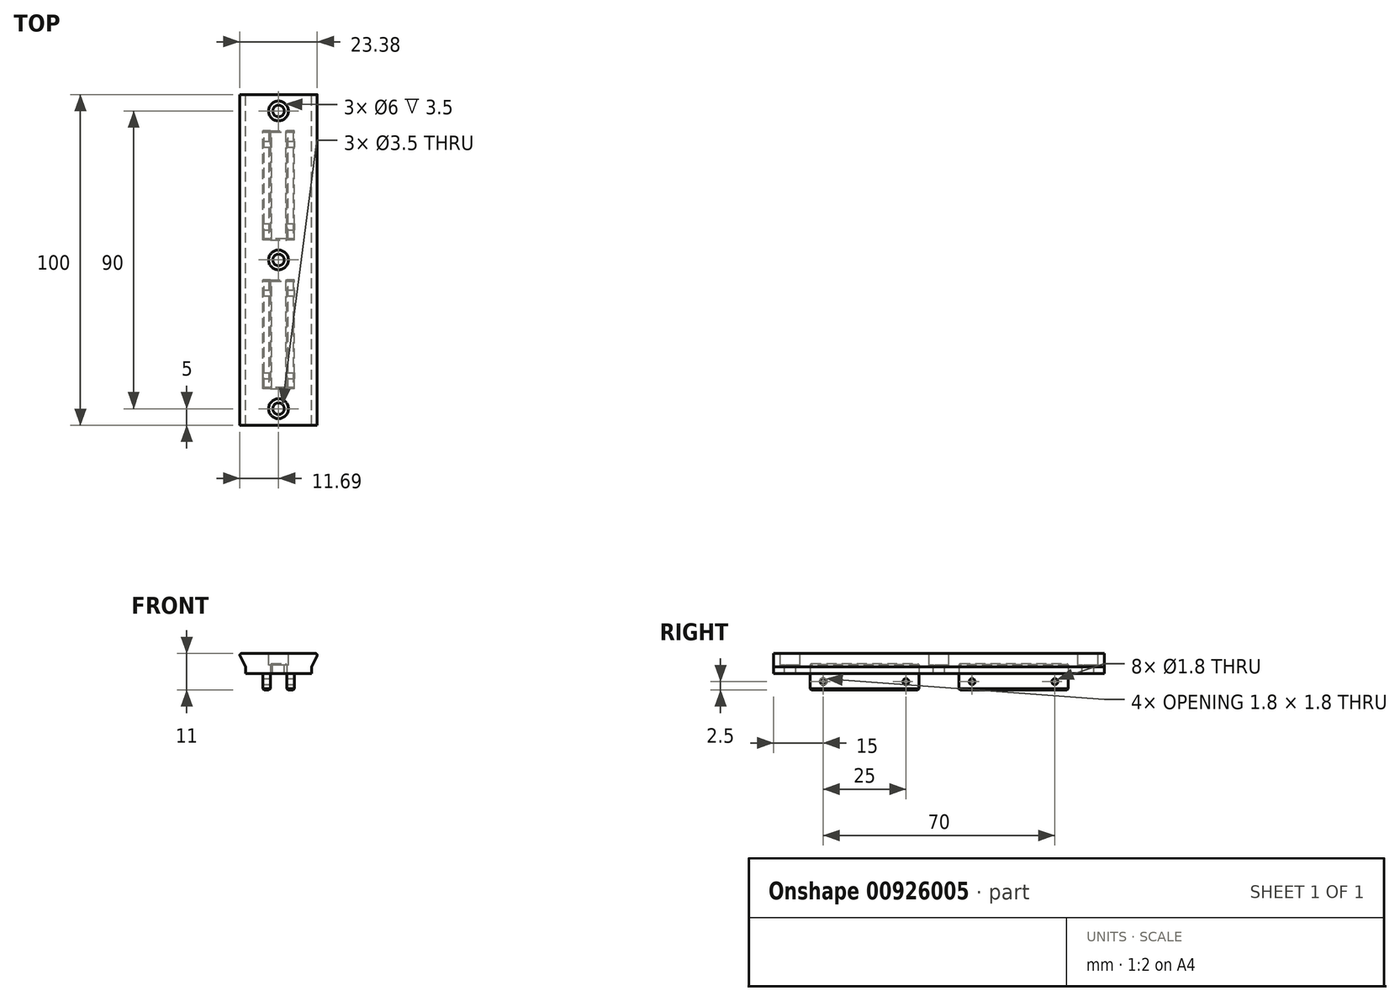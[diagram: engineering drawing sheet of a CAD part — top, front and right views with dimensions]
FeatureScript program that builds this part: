
annotation { "Feature Type Name" : "Feature", "Feature Type Description" : "" }
export const myFeature = defineFeature(function(context is Context, id is Id, definition is map)
    precondition{}
    {
        {
            var Q0;
            Q0=qCreatedBy(makeId("Front.planeOp"),FACE);
            var sketch = newSketch(context, id + "F0", { "sketchPlane" : qUnion([Q0])});
            skLineSegment(sketch, "E0.top", {"start": v(4.75, -2.5) * mm, "end": v(-4.75, -2.5) * mm});
            skLineSegment(sketch, "E0.left", {"start": v(4.75, 2.5) * mm, "end": v(4.75, -2.5) * mm});
            skLineSegment(sketch, "E0.right", {"start": v(-4.75, 2.5) * mm, "end": v(-4.75, -2.5) * mm});
            skPoint(sketch, "E0.middle", {"position": v(0, 0) * mm});
            skLineSegment(sketch, "E1.left", {"start": v(10, 4.5) * mm, "end": v(10, 2.5) * mm});
            skLineSegment(sketch, "E1.right", {"start": v(-10, 4.5) * mm, "end": v(-10, 2.5) * mm});
            skPoint(sketch, "E1.middle", {"position": v(0, 2.5) * mm});
            skLineSegment(sketch, "E2", {"start": v(-4.75, 2.5) * mm, "end": v(-10, 2.5) * mm});
            skLineSegment(sketch, "E3", {"start": v(4.75, 2.5) * mm, "end": v(10, 2.5) * mm});
            skPoint(sketch, "E4.orphan", {"position": v(-10, 0.5) * mm});
            skPoint(sketch, "E5.orphan", {"position": v(10, 0.5) * mm});
            skLineSegment(sketch, "E6.bottom", {"start": v(10, 8.5) * mm, "end": v(-10, 8.5) * mm});
            skPoint(sketch, "E6.middle", {"position": v(0, 4.5) * mm});
            skLineSegment(sketch, "E7.bottom", {"start": v(-10, 8.5) * mm, "end": v(-6, 8.5) * mm});
            skLineSegment(sketch, "E8.bottom", {"start": v(10, 8.5) * mm, "end": v(6, 8.5) * mm});
            skLineSegment(sketch, "E9.bottom", {"start": v(-2.5, -2.5) * mm, "end": v(2.5, -2.5) * mm});
            skLineSegment(sketch, "E9.top", {"start": v(-2.5, 2.5) * mm, "end": v(2.5, 2.5) * mm});
            skLineSegment(sketch, "E9.left", {"start": v(-2.5, -2.5) * mm, "end": v(-2.5, 2.5) * mm});
            skLineSegment(sketch, "E9.right", {"start": v(2.5, -2.5) * mm, "end": v(2.5, 2.5) * mm});
            skLineSegment(sketch, "E10", {"start": v(-10, 8.5) * mm, "end": v(-12, 8.5) * mm});
            skLineSegment(sketch, "E11", {"start": v(10, 8.5) * mm, "end": v(12, 8.5) * mm});
            skLineSegment(sketch, "E12", {"start": v(-12, 8.5) * mm, "end": v(-10, 4.5) * mm});
            skLineSegment(sketch, "E13", {"start": v(12, 8.5) * mm, "end": v(10, 4.5) * mm});
            skSolve(sketch);
        }
        {
            var Q0;
            {var subQ0=sQuery(id+"F0.wireOp",EDGE,"E0.left");Q0=makeQuery(id+"F0.imprint","IMPRINT",FACE,{"disambiguationData":[TD([[makeQuery(id+"F0.imprint","IMPRINT",EDGE,{"derivedFrom":subQ0}),-1.0]])]});}
            extrude(context, id + "F1", {"entities" : qUnion([Q0]), "depth" : 100 * mm, "offsetDistance" : 25 * mm});
        }
        {
            var Q0;
            Q0=makeQuery(id+"F1.opExtrude","SWEPT_FACE",FACE,{"disambiguationData":[OSD([sQuery(id+"F0.wireOp",EDGE,"E9.top")])]});
            var sketch = newSketch(context, id + "F2", { "sketchPlane" : qUnion([Q0])});
            skLineSegment(sketch, "E14", {"start": v(-2.5, 10) * mm, "end": v(2.5, 10) * mm});
            skLineSegment(sketch, "E15", {"start": v(2.5, 90) * mm, "end": v(-2.5, 90) * mm});
            skLineSegment(sketch, "E16.top", {"start": v(-2.5, 55) * mm, "end": v(2.5, 55) * mm});
            skLineSegment(sketch, "E16.left", {"start": v(-2.5, 50) * mm, "end": v(-2.5, 55) * mm});
            skLineSegment(sketch, "E16.right", {"start": v(2.5, 50) * mm, "end": v(2.5, 55) * mm});
            skLineSegment(sketch, "E17.top", {"start": v(2.5, 45) * mm, "end": v(-2.5, 45) * mm});
            skLineSegment(sketch, "E17.left", {"start": v(2.5, 50) * mm, "end": v(2.5, 45) * mm});
            skLineSegment(sketch, "E17.right", {"start": v(-2.5, 50) * mm, "end": v(-2.5, 45) * mm});
            skSolve(sketch);
        }
        {
            var Q0;
            {var subQ0=sQuery(id+"F2.wireOp",EDGE,"E15");Q0=makeQuery(id+"F2.imprint","IMPRINT",FACE,{"disambiguationData":[TD([[makeQuery(id+"F2.imprint","IMPRINT",EDGE,{"derivedFrom":subQ0}),-1.0]])]});}
            var Q1;
            Q1=makeQuery(id+"F2.imprint","IMPRINT",FACE,{"disambiguationData":[TD([[makeQuery(id+"F2.imprint","IMPRINT",EDGE,{"derivedFrom":sQuery(id+"F2.wireOp",EDGE,"E16.top")}),-1.0]])]});
            var Q2;
            {var subQ0=sQuery(id+"F2.wireOp",EDGE,"E14");Q2=makeQuery(id+"F2.imprint","IMPRINT",FACE,{"disambiguationData":[TD([[makeQuery(id+"F2.imprint","IMPRINT",EDGE,{"derivedFrom":subQ0}),-1.0]])]});}
            extrude(context, id + "F3", {"entities" : qUnion([Q0, Q1, Q2]), "operationType" : NewBodyOperationType.ADD, "depth" : 5 * mm, "offsetDistance" : 25 * mm});
        }
        {
            var Q0;
            Q0=makeQuery(id+"F1.opExtrude","SWEPT_FACE",FACE,{"disambiguationData":[OSD([sQuery(id+"F0.wireOp",EDGE,"E0.left")])]});
            var sketch = newSketch(context, id + "F4", { "sketchPlane" : qUnion([Q0])});
            skLineSegment(sketch, "E18", {"start": v(-100, 2.5) * mm, "end": v(-100, -19) * mm});
            skLineSegment(sketch, "E19", {"start": v(-100, -19) * mm, "end": v(0, -19) * mm});
            skLineSegment(sketch, "E20", {"start": v(0, -19) * mm, "end": v(0, 2.5) * mm});
            skCircle(sketch, "E21", {"center": v(-85, 0) * mm, "radius": 0.9 * mm});
            skCircle(sketch, "E22", {"center": v(-40, 0) * mm, "radius": 0.9 * mm});
            skLineSegment(sketch, "E23", {"start": v(-40, 0) * mm, "end": v(0, 0) * mm});
            skCircle(sketch, "E24", {"center": v(-15, 0) * mm, "radius": 0.9 * mm});
            skCircle(sketch, "E25", {"center": v(-60, 0) * mm, "radius": 0.9 * mm});
            skSolve(sketch);
        }
        {
            var Q0;
            Q0=qSketchRegion(id+"F4",true);
            extrude(context, id + "F5", {"entities" : qUnion([Q0]), "operationType" : NewBodyOperationType.REMOVE, "oppositeDirection" : true, "depth" : 25 * mm, "offsetDistance" : 25 * mm});
        }
        {
            var Q0;
            Q0=makeQuery(id+"F1.opExtrude","SWEPT_FACE",FACE,{"disambiguationData":[OSD([sQuery(id+"F0.wireOp",EDGE,"E6.bottom"),sQuery(id+"F0.wireOp",EDGE,"E7.bottom"),sQuery(id+"F0.wireOp",EDGE,"E8.bottom")])]});
            var sketch = newSketch(context, id + "F6", { "sketchPlane" : qUnion([Q0])});
            skLineSegment(sketch, "E26", {"start": v(0, -100) * mm, "end": v(0, -95) * mm});
            skLineSegment(sketch, "E27", {"start": v(0, 0) * mm, "end": v(0, -5) * mm});
            skLineSegment(sketch, "E28", {"start": v(0, -5) * mm, "end": v(0, -95) * mm});
            skCircle(sketch, "E29", {"center": v(0, -50) * mm, "radius": 3 * mm});
            skCircle(sketch, "E30", {"center": v(0, -5) * mm, "radius": 3 * mm});
            skCircle(sketch, "E31", {"center": v(0, -95) * mm, "radius": 3 * mm});
            skCircle(sketch, "E32", {"center": v(0, -5) * mm, "radius": 1.75 * mm});
            skCircle(sketch, "E33", {"center": v(0, -50) * mm, "radius": 1.75 * mm});
            skCircle(sketch, "E34", {"center": v(0, -95) * mm, "radius": 1.75 * mm});
            skSolve(sketch);
        }
        {
            var Q0;
            Q0=qSketchRegion(id+"F6",true);
            extrude(context, id + "F7", {"entities" : qUnion([Q0]), "operationType" : NewBodyOperationType.REMOVE, "oppositeDirection" : true, "depth" : 3.5 * mm, "offsetDistance" : 25 * mm});
        }
        {
            var Q0;
            Q0=makeQuery(id+"F7.boolean.opBoolean","SPLIT",FACE,{"disambiguationData":[TD([makeQuery(id+"F7.opExtrude","SWEPT_FACE",FACE,{"disambiguationData":[OSD([sQuery(id+"F6.wireOp",EDGE,"E32")])]})])],"derivedFrom":makeQuery(id+"F1.opExtrude","SWEPT_FACE",FACE,{"disambiguationData":[OSD([sQuery(id+"F0.wireOp",EDGE,"E6.bottom"),sQuery(id+"F0.wireOp",EDGE,"E7.bottom"),sQuery(id+"F0.wireOp",EDGE,"E8.bottom")])]})});
            var Q1;
            Q1=makeQuery(id+"F7.boolean.opBoolean","SPLIT",FACE,{"disambiguationData":[TD([makeQuery(id+"F7.opExtrude","SWEPT_FACE",FACE,{"disambiguationData":[OSD([sQuery(id+"F6.wireOp",EDGE,"E33")])]})])],"derivedFrom":makeQuery(id+"F1.opExtrude","SWEPT_FACE",FACE,{"disambiguationData":[OSD([sQuery(id+"F0.wireOp",EDGE,"E6.bottom"),sQuery(id+"F0.wireOp",EDGE,"E7.bottom"),sQuery(id+"F0.wireOp",EDGE,"E8.bottom")])]})});
            var Q2;
            Q2=makeQuery(id+"F7.boolean.opBoolean","SPLIT",FACE,{"disambiguationData":[TD([makeQuery(id+"F7.opExtrude","SWEPT_FACE",FACE,{"disambiguationData":[OSD([sQuery(id+"F6.wireOp",EDGE,"E34")])]})])],"derivedFrom":makeQuery(id+"F1.opExtrude","SWEPT_FACE",FACE,{"disambiguationData":[OSD([sQuery(id+"F0.wireOp",EDGE,"E6.bottom"),sQuery(id+"F0.wireOp",EDGE,"E7.bottom"),sQuery(id+"F0.wireOp",EDGE,"E8.bottom")])]})});
            extrude(context, id + "F8", {"entities" : qUnion([Q0, Q1, Q2]), "operationType" : NewBodyOperationType.REMOVE, "endBound" : BoundingType.THROUGH_ALL, "oppositeDirection" : true, "depth" : 25 * mm, "offsetDistance" : 25 * mm});
        }
        {
            var Q0;
            Q0=makeQuery(id+"F7.boolean.opBoolean","COPY",EDGE,{"derivedFrom":makeQuery(id+"F7.opExtrude","CAP_EDGE",EDGE,{"disambiguationData":[OSD([sQuery(id+"F6.wireOp",EDGE,"E30")])],"isStart":true})});
            var Q1;
            Q1=makeQuery(id+"F7.boolean.opBoolean","COPY",EDGE,{"derivedFrom":makeQuery(id+"F7.opExtrude","CAP_EDGE",EDGE,{"disambiguationData":[OSD([sQuery(id+"F6.wireOp",EDGE,"E29")])],"isStart":true})});
            var Q2;
            Q2=makeQuery(id+"F7.boolean.opBoolean","COPY",EDGE,{"derivedFrom":makeQuery(id+"F7.opExtrude","CAP_EDGE",EDGE,{"disambiguationData":[OSD([sQuery(id+"F6.wireOp",EDGE,"E31")])],"isStart":true})});
            var Q3;
            Q3=makeQuery(id+"F7.boolean.opBoolean","COPY",EDGE,{"derivedFrom":makeQuery(id+"F7.opExtrude","CAP_EDGE",EDGE,{"disambiguationData":[OSD([sQuery(id+"F6.wireOp",EDGE,"E32")])],"isStart":false})});
            var Q4;
            Q4=makeQuery(id+"F7.boolean.opBoolean","COPY",EDGE,{"derivedFrom":makeQuery(id+"F7.opExtrude","CAP_EDGE",EDGE,{"disambiguationData":[OSD([sQuery(id+"F6.wireOp",EDGE,"E33")])],"isStart":false})});
            var Q5;
            Q5=makeQuery(id+"F7.boolean.opBoolean","COPY",EDGE,{"derivedFrom":makeQuery(id+"F7.opExtrude","CAP_EDGE",EDGE,{"disambiguationData":[OSD([sQuery(id+"F6.wireOp",EDGE,"E34")])],"isStart":false})});
            var Q6;
            {var subQ0=sQuery(id+"F0.wireOp",EDGE,"E9.right");var subQ1=sQuery(id+"F0.wireOp",EDGE,"E9.left");var subQ2=sQuery(id+"F0.wireOp",EDGE,"E9.top");var subQ3=sQuery(id+"F0.wireOp",EDGE,"E0.top");Q6=makeQuery(id+"F8.boolean.opBoolean","INTERSECT",EDGE,{"derivedFrom":[makeQuery(id+"F3.boolean.opBoolean","MERGE",FACE,{"derivedFrom":[makeQuery(id+"F1.opExtrude","SWEPT_FACE",FACE,{"disambiguationData":[OSD([subQ3]),TDD([makeQuery(id+"F0.imprint","IMPRINT",EDGE,{"disambiguationData":[TD([[makeQuery(id+"F0.imprint","INTERSECT",VERTEX,{"derivedFrom":[subQ3,sQuery(id+"F0.wireOp",EDGE,"E0.left")]}),-1.0]])],"derivedFrom":subQ3})])]}),makeQuery(id+"F1.opExtrude","SWEPT_FACE",FACE,{"disambiguationData":[OSD([subQ3]),TDD([makeQuery(id+"F0.imprint","IMPRINT",EDGE,{"disambiguationData":[TD([[makeQuery(id+"F0.imprint","INTERSECT",VERTEX,{"derivedFrom":[subQ3,sQuery(id+"F0.wireOp",EDGE,"E0.right")]}),1.0]])],"derivedFrom":subQ3})])]}),makeQuery(id+"F3.opExtrude","CAP_FACE",FACE,{"disambiguationData":[OSD([subQ2,subQ1,subQ0,sQuery(id+"F2.wireOp",EDGE,"E14")])],"isStart":false}),makeQuery(id+"F3.opExtrude","CAP_FACE",FACE,{"disambiguationData":[OSD([subQ2,subQ1,subQ0,sQuery(id+"F2.wireOp",EDGE,"E15")])],"isStart":false}),makeQuery(id+"F3.opExtrude","CAP_FACE",FACE,{"disambiguationData":[OSD([sQuery(id+"F2.wireOp",EDGE,"E16.top"),sQuery(id+"F2.wireOp",EDGE,"E16.left"),sQuery(id+"F2.wireOp",EDGE,"E16.right"),sQuery(id+"F2.wireOp",EDGE,"E17.top"),sQuery(id+"F2.wireOp",EDGE,"E17.left"),sQuery(id+"F2.wireOp",EDGE,"E17.right")])],"isStart":false})]}),makeQuery(id+"F8.opExtrude","SWEPT_FACE",FACE,{"disambiguationData":[OSD([sQuery(id+"F6.wireOp",EDGE,"E34")])]})]});}
            var Q7;
            {var subQ0=sQuery(id+"F0.wireOp",EDGE,"E9.right");var subQ1=sQuery(id+"F0.wireOp",EDGE,"E9.left");var subQ2=sQuery(id+"F0.wireOp",EDGE,"E9.top");var subQ3=sQuery(id+"F0.wireOp",EDGE,"E0.top");Q7=makeQuery(id+"F8.boolean.opBoolean","INTERSECT",EDGE,{"derivedFrom":[makeQuery(id+"F3.boolean.opBoolean","MERGE",FACE,{"derivedFrom":[makeQuery(id+"F1.opExtrude","SWEPT_FACE",FACE,{"disambiguationData":[OSD([subQ3]),TDD([makeQuery(id+"F0.imprint","IMPRINT",EDGE,{"disambiguationData":[TD([[makeQuery(id+"F0.imprint","INTERSECT",VERTEX,{"derivedFrom":[subQ3,sQuery(id+"F0.wireOp",EDGE,"E0.left")]}),-1.0]])],"derivedFrom":subQ3})])]}),makeQuery(id+"F1.opExtrude","SWEPT_FACE",FACE,{"disambiguationData":[OSD([subQ3]),TDD([makeQuery(id+"F0.imprint","IMPRINT",EDGE,{"disambiguationData":[TD([[makeQuery(id+"F0.imprint","INTERSECT",VERTEX,{"derivedFrom":[subQ3,sQuery(id+"F0.wireOp",EDGE,"E0.right")]}),1.0]])],"derivedFrom":subQ3})])]}),makeQuery(id+"F3.opExtrude","CAP_FACE",FACE,{"disambiguationData":[OSD([subQ2,subQ1,subQ0,sQuery(id+"F2.wireOp",EDGE,"E14")])],"isStart":false}),makeQuery(id+"F3.opExtrude","CAP_FACE",FACE,{"disambiguationData":[OSD([subQ2,subQ1,subQ0,sQuery(id+"F2.wireOp",EDGE,"E15")])],"isStart":false}),makeQuery(id+"F3.opExtrude","CAP_FACE",FACE,{"disambiguationData":[OSD([sQuery(id+"F2.wireOp",EDGE,"E16.top"),sQuery(id+"F2.wireOp",EDGE,"E16.left"),sQuery(id+"F2.wireOp",EDGE,"E16.right"),sQuery(id+"F2.wireOp",EDGE,"E17.top"),sQuery(id+"F2.wireOp",EDGE,"E17.left"),sQuery(id+"F2.wireOp",EDGE,"E17.right")])],"isStart":false})]}),makeQuery(id+"F8.opExtrude","SWEPT_FACE",FACE,{"disambiguationData":[OSD([sQuery(id+"F6.wireOp",EDGE,"E33")])]})]});}
            var Q8;
            {var subQ0=sQuery(id+"F0.wireOp",EDGE,"E9.right");var subQ1=sQuery(id+"F0.wireOp",EDGE,"E9.left");var subQ2=sQuery(id+"F0.wireOp",EDGE,"E9.top");var subQ3=sQuery(id+"F0.wireOp",EDGE,"E0.top");Q8=makeQuery(id+"F8.boolean.opBoolean","INTERSECT",EDGE,{"derivedFrom":[makeQuery(id+"F3.boolean.opBoolean","MERGE",FACE,{"derivedFrom":[makeQuery(id+"F1.opExtrude","SWEPT_FACE",FACE,{"disambiguationData":[OSD([subQ3]),TDD([makeQuery(id+"F0.imprint","IMPRINT",EDGE,{"disambiguationData":[TD([[makeQuery(id+"F0.imprint","INTERSECT",VERTEX,{"derivedFrom":[subQ3,sQuery(id+"F0.wireOp",EDGE,"E0.left")]}),-1.0]])],"derivedFrom":subQ3})])]}),makeQuery(id+"F1.opExtrude","SWEPT_FACE",FACE,{"disambiguationData":[OSD([subQ3]),TDD([makeQuery(id+"F0.imprint","IMPRINT",EDGE,{"disambiguationData":[TD([[makeQuery(id+"F0.imprint","INTERSECT",VERTEX,{"derivedFrom":[subQ3,sQuery(id+"F0.wireOp",EDGE,"E0.right")]}),1.0]])],"derivedFrom":subQ3})])]}),makeQuery(id+"F3.opExtrude","CAP_FACE",FACE,{"disambiguationData":[OSD([subQ2,subQ1,subQ0,sQuery(id+"F2.wireOp",EDGE,"E14")])],"isStart":false}),makeQuery(id+"F3.opExtrude","CAP_FACE",FACE,{"disambiguationData":[OSD([subQ2,subQ1,subQ0,sQuery(id+"F2.wireOp",EDGE,"E15")])],"isStart":false}),makeQuery(id+"F3.opExtrude","CAP_FACE",FACE,{"disambiguationData":[OSD([sQuery(id+"F2.wireOp",EDGE,"E16.top"),sQuery(id+"F2.wireOp",EDGE,"E16.left"),sQuery(id+"F2.wireOp",EDGE,"E16.right"),sQuery(id+"F2.wireOp",EDGE,"E17.top"),sQuery(id+"F2.wireOp",EDGE,"E17.left"),sQuery(id+"F2.wireOp",EDGE,"E17.right")])],"isStart":false})]}),makeQuery(id+"F8.opExtrude","SWEPT_FACE",FACE,{"disambiguationData":[OSD([sQuery(id+"F6.wireOp",EDGE,"E32")])]})]});}
            chamfer(context, id + "F9", {"entities" : qUnion([Q0, Q1, Q2, Q3, Q4, Q5, Q6, Q7, Q8]), "width" : 0.5 * mm, "tangentPropagation" : true});
        }
        {
            var Q0;
            Q0=makeQuery(id+"F1.opExtrude","SWEPT_FACE",FACE,{"disambiguationData":[OSD([sQuery(id+"F0.wireOp",EDGE,"E0.right")])]});
            var sketch = newSketch(context, id + "F10", { "sketchPlane" : qUnion([Q0])});
            skLineSegment(sketch, "E35.bottom", {"start": v(0, 2.5) * mm, "end": v(11, 2.5) * mm});
            skLineSegment(sketch, "E35.top", {"start": v(0, -2.5) * mm, "end": v(11, -2.5) * mm});
            skLineSegment(sketch, "E35.left", {"start": v(0, 2.5) * mm, "end": v(0, -2.5) * mm});
            skLineSegment(sketch, "E35.right", {"start": v(11, 2.5) * mm, "end": v(11, -2.5) * mm});
            skLineSegment(sketch, "E36.bottom", {"start": v(44, 2.5) * mm, "end": v(56, 2.5) * mm});
            skLineSegment(sketch, "E36.top", {"start": v(44, -2.5) * mm, "end": v(56, -2.5) * mm});
            skLineSegment(sketch, "E36.left", {"start": v(44, 2.5) * mm, "end": v(44, -2.5) * mm});
            skLineSegment(sketch, "E36.right", {"start": v(56, 2.5) * mm, "end": v(56, -2.5) * mm});
            skLineSegment(sketch, "E37.bottom", {"start": v(100, 2.5) * mm, "end": v(89, 2.5) * mm});
            skLineSegment(sketch, "E37.top", {"start": v(100, -2.5) * mm, "end": v(89, -2.5) * mm});
            skLineSegment(sketch, "E37.left", {"start": v(100, 2.5) * mm, "end": v(100, -2.5) * mm});
            skLineSegment(sketch, "E37.right", {"start": v(89, 2.5) * mm, "end": v(89, -2.5) * mm});
            skSolve(sketch);
        }
        {
            var Q0;
            Q0=qSketchRegion(id+"F10",true);
            extrude(context, id + "F11", {"entities" : qUnion([Q0]), "operationType" : NewBodyOperationType.REMOVE, "oppositeDirection" : true, "depth" : 25 * mm, "offsetDistance" : 25 * mm});
        }
        {
            var Q0;
            {var subQ0=sQuery(id+"F0.wireOp",EDGE,"E0.right");var subQ1=sQuery(id+"F0.wireOp",EDGE,"E9.left");var subQ2=sQuery(id+"F0.wireOp",EDGE,"E9.right");var subQ3=sQuery(id+"F0.wireOp",EDGE,"E9.top");var subQ4=sQuery(id+"F0.wireOp",EDGE,"E0.top");Q0=makeQuery(id+"F11.boolean.opBoolean","SPLIT",FACE,{"disambiguationData":[TD([makeQuery(id+"F1.opExtrude","SWEPT_FACE",FACE,{"disambiguationData":[OSD([subQ0])]}),makeQuery(id+"F1.opExtrude","SWEPT_FACE",FACE,{"disambiguationData":[OSD([subQ1])]}),makeQuery(id+"F11.opExtrude","SWEPT_FACE",FACE,{"disambiguationData":[OSD([sQuery(id+"F10.wireOp",EDGE,"E36.right")])]}),makeQuery(id+"F11.opExtrude","SWEPT_FACE",FACE,{"disambiguationData":[OSD([sQuery(id+"F10.wireOp",EDGE,"E37.right")])]})])],"derivedFrom":makeQuery(id+"F3.boolean.opBoolean","MERGE",FACE,{"derivedFrom":[makeQuery(id+"F1.opExtrude","SWEPT_FACE",FACE,{"disambiguationData":[OSD([subQ4]),TDD([makeQuery(id+"F0.imprint","IMPRINT",EDGE,{"disambiguationData":[TD([[makeQuery(id+"F0.imprint","INTERSECT",VERTEX,{"derivedFrom":[subQ4,sQuery(id+"F0.wireOp",EDGE,"E0.left")]}),-1.0]])],"derivedFrom":subQ4})])]}),makeQuery(id+"F1.opExtrude","SWEPT_FACE",FACE,{"disambiguationData":[OSD([subQ4]),TDD([makeQuery(id+"F0.imprint","IMPRINT",EDGE,{"disambiguationData":[TD([[makeQuery(id+"F0.imprint","INTERSECT",VERTEX,{"derivedFrom":[subQ4,subQ0]}),1.0]])],"derivedFrom":subQ4})])]}),makeQuery(id+"F3.opExtrude","CAP_FACE",FACE,{"disambiguationData":[OSD([subQ3,subQ1,subQ2,sQuery(id+"F2.wireOp",EDGE,"E14")])],"isStart":false}),makeQuery(id+"F3.opExtrude","CAP_FACE",FACE,{"disambiguationData":[OSD([subQ3,subQ1,subQ2,sQuery(id+"F2.wireOp",EDGE,"E15")])],"isStart":false}),makeQuery(id+"F3.opExtrude","CAP_FACE",FACE,{"disambiguationData":[OSD([sQuery(id+"F2.wireOp",EDGE,"E16.top"),sQuery(id+"F2.wireOp",EDGE,"E16.left"),sQuery(id+"F2.wireOp",EDGE,"E16.right"),sQuery(id+"F2.wireOp",EDGE,"E17.top"),sQuery(id+"F2.wireOp",EDGE,"E17.left"),sQuery(id+"F2.wireOp",EDGE,"E17.right")])],"isStart":false})]})});}
            var sketch = newSketch(context, id + "F12", { "sketchPlane" : qUnion([Q0])});
            skLineSegment(sketch, "E38.bottom", {"start": v(-2.5, 89) * mm, "end": v(2.5, 89) * mm});
            skLineSegment(sketch, "E38.top", {"start": v(-2.5, 56) * mm, "end": v(2.5, 56) * mm});
            skLineSegment(sketch, "E38.left", {"start": v(-2.5, 89) * mm, "end": v(-2.5, 56) * mm});
            skLineSegment(sketch, "E38.right", {"start": v(2.5, 89) * mm, "end": v(2.5, 56) * mm});
            skSolve(sketch);
        }
        {
            var Q0;
            Q0 = qSketchRegion(id + "F12", true);
            extrude(context, id + "F13", {"entities" : qUnion([Q0]), "operationType" : NewBodyOperationType.REMOVE, "oppositeDirection" : true, "depth" : 8 * mm, "offsetDistance" : 25 * mm});
        }
        {
            var Q0;
            {var subQ0=sQuery(id+"F0.wireOp",EDGE,"E0.right");var subQ1=sQuery(id+"F0.wireOp",EDGE,"E9.left");var subQ2=sQuery(id+"F0.wireOp",EDGE,"E9.right");var subQ3=sQuery(id+"F0.wireOp",EDGE,"E9.top");var subQ4=sQuery(id+"F0.wireOp",EDGE,"E0.top");Q0=makeQuery(id+"F11.boolean.opBoolean","SPLIT",FACE,{"disambiguationData":[TD([makeQuery(id+"F1.opExtrude","SWEPT_FACE",FACE,{"disambiguationData":[OSD([subQ0])]}),makeQuery(id+"F1.opExtrude","SWEPT_FACE",FACE,{"disambiguationData":[OSD([subQ1])]}),makeQuery(id+"F11.opExtrude","SWEPT_FACE",FACE,{"disambiguationData":[OSD([sQuery(id+"F10.wireOp",EDGE,"E35.right")])]}),makeQuery(id+"F11.opExtrude","SWEPT_FACE",FACE,{"disambiguationData":[OSD([sQuery(id+"F10.wireOp",EDGE,"E36.left")])]})])],"derivedFrom":makeQuery(id+"F3.boolean.opBoolean","MERGE",FACE,{"derivedFrom":[makeQuery(id+"F1.opExtrude","SWEPT_FACE",FACE,{"disambiguationData":[OSD([subQ4]),TDD([makeQuery(id+"F0.imprint","IMPRINT",EDGE,{"disambiguationData":[TD([[makeQuery(id+"F0.imprint","INTERSECT",VERTEX,{"derivedFrom":[subQ4,sQuery(id+"F0.wireOp",EDGE,"E0.left")]}),-1.0]])],"derivedFrom":subQ4})])]}),makeQuery(id+"F1.opExtrude","SWEPT_FACE",FACE,{"disambiguationData":[OSD([subQ4]),TDD([makeQuery(id+"F0.imprint","IMPRINT",EDGE,{"disambiguationData":[TD([[makeQuery(id+"F0.imprint","INTERSECT",VERTEX,{"derivedFrom":[subQ4,subQ0]}),1.0]])],"derivedFrom":subQ4})])]}),makeQuery(id+"F3.opExtrude","CAP_FACE",FACE,{"disambiguationData":[OSD([subQ3,subQ1,subQ2,sQuery(id+"F2.wireOp",EDGE,"E14")])],"isStart":false}),makeQuery(id+"F3.opExtrude","CAP_FACE",FACE,{"disambiguationData":[OSD([subQ3,subQ1,subQ2,sQuery(id+"F2.wireOp",EDGE,"E15")])],"isStart":false}),makeQuery(id+"F3.opExtrude","CAP_FACE",FACE,{"disambiguationData":[OSD([sQuery(id+"F2.wireOp",EDGE,"E16.top"),sQuery(id+"F2.wireOp",EDGE,"E16.left"),sQuery(id+"F2.wireOp",EDGE,"E16.right"),sQuery(id+"F2.wireOp",EDGE,"E17.top"),sQuery(id+"F2.wireOp",EDGE,"E17.left"),sQuery(id+"F2.wireOp",EDGE,"E17.right")])],"isStart":false})]})});}
            var sketch = newSketch(context, id + "F14", { "sketchPlane" : qUnion([Q0])});
            skLineSegment(sketch, "E39.bottom", {"start": v(-2.5, 44) * mm, "end": v(2.5, 44) * mm});
            skLineSegment(sketch, "E39.top", {"start": v(-2.5, 11) * mm, "end": v(2.5, 11) * mm});
            skLineSegment(sketch, "E39.left", {"start": v(-2.5, 44) * mm, "end": v(-2.5, 11) * mm});
            skLineSegment(sketch, "E39.right", {"start": v(2.5, 44) * mm, "end": v(2.5, 11) * mm});
            skSolve(sketch);
        }
        {
            var Q0;
            Q0 = qSketchRegion(id + "F14", true);
            extrude(context, id + "F15", {"entities" : qUnion([Q0]), "operationType" : NewBodyOperationType.REMOVE, "oppositeDirection" : true, "depth" : 8 * mm, "offsetDistance" : 25 * mm});
        }
        {
            var Q0;
            {var subQ0=sQuery(id+"F0.wireOp",EDGE,"E0.right");var subQ1=sQuery(id+"F0.wireOp",EDGE,"E9.left");var subQ2=sQuery(id+"F0.wireOp",EDGE,"E9.right");var subQ3=sQuery(id+"F0.wireOp",EDGE,"E9.top");var subQ4=sQuery(id+"F0.wireOp",EDGE,"E0.top");Q0=makeQuery(id+"F11.boolean.opBoolean","SPLIT",FACE,{"disambiguationData":[TD([makeQuery(id+"F1.opExtrude","SWEPT_FACE",FACE,{"disambiguationData":[OSD([subQ0])]}),makeQuery(id+"F1.opExtrude","SWEPT_FACE",FACE,{"disambiguationData":[OSD([subQ1])]}),makeQuery(id+"F11.opExtrude","SWEPT_FACE",FACE,{"disambiguationData":[OSD([sQuery(id+"F10.wireOp",EDGE,"E35.right")])]}),makeQuery(id+"F11.opExtrude","SWEPT_FACE",FACE,{"disambiguationData":[OSD([sQuery(id+"F10.wireOp",EDGE,"E36.left")])]})])],"derivedFrom":makeQuery(id+"F3.boolean.opBoolean","MERGE",FACE,{"derivedFrom":[makeQuery(id+"F1.opExtrude","SWEPT_FACE",FACE,{"disambiguationData":[OSD([subQ4]),TDD([makeQuery(id+"F0.imprint","IMPRINT",EDGE,{"disambiguationData":[TD([[makeQuery(id+"F0.imprint","INTERSECT",VERTEX,{"derivedFrom":[subQ4,sQuery(id+"F0.wireOp",EDGE,"E0.left")]}),-1.0]])],"derivedFrom":subQ4})])]}),makeQuery(id+"F1.opExtrude","SWEPT_FACE",FACE,{"disambiguationData":[OSD([subQ4]),TDD([makeQuery(id+"F0.imprint","IMPRINT",EDGE,{"disambiguationData":[TD([[makeQuery(id+"F0.imprint","INTERSECT",VERTEX,{"derivedFrom":[subQ4,subQ0]}),1.0]])],"derivedFrom":subQ4})])]}),makeQuery(id+"F3.opExtrude","CAP_FACE",FACE,{"disambiguationData":[OSD([subQ3,subQ1,subQ2,sQuery(id+"F2.wireOp",EDGE,"E14")])],"isStart":false}),makeQuery(id+"F3.opExtrude","CAP_FACE",FACE,{"disambiguationData":[OSD([subQ3,subQ1,subQ2,sQuery(id+"F2.wireOp",EDGE,"E15")])],"isStart":false}),makeQuery(id+"F3.opExtrude","CAP_FACE",FACE,{"disambiguationData":[OSD([sQuery(id+"F2.wireOp",EDGE,"E16.top"),sQuery(id+"F2.wireOp",EDGE,"E16.left"),sQuery(id+"F2.wireOp",EDGE,"E16.right"),sQuery(id+"F2.wireOp",EDGE,"E17.top"),sQuery(id+"F2.wireOp",EDGE,"E17.left"),sQuery(id+"F2.wireOp",EDGE,"E17.right")])],"isStart":false})]})});}
            var Q1;
            {var subQ0=sQuery(id+"F0.wireOp",EDGE,"E0.left");var subQ1=sQuery(id+"F0.wireOp",EDGE,"E9.right");var subQ2=sQuery(id+"F0.wireOp",EDGE,"E9.left");var subQ3=sQuery(id+"F0.wireOp",EDGE,"E9.top");var subQ4=sQuery(id+"F0.wireOp",EDGE,"E0.top");Q1=makeQuery(id+"F11.boolean.opBoolean","SPLIT",FACE,{"disambiguationData":[TD([makeQuery(id+"F1.opExtrude","SWEPT_FACE",FACE,{"disambiguationData":[OSD([subQ0])]}),makeQuery(id+"F1.opExtrude","SWEPT_FACE",FACE,{"disambiguationData":[OSD([subQ1])]}),makeQuery(id+"F11.opExtrude","SWEPT_FACE",FACE,{"disambiguationData":[OSD([sQuery(id+"F10.wireOp",EDGE,"E35.right")])]}),makeQuery(id+"F11.opExtrude","SWEPT_FACE",FACE,{"disambiguationData":[OSD([sQuery(id+"F10.wireOp",EDGE,"E36.left")])]})])],"derivedFrom":makeQuery(id+"F3.boolean.opBoolean","MERGE",FACE,{"derivedFrom":[makeQuery(id+"F1.opExtrude","SWEPT_FACE",FACE,{"disambiguationData":[OSD([subQ4]),TDD([makeQuery(id+"F0.imprint","IMPRINT",EDGE,{"disambiguationData":[TD([[makeQuery(id+"F0.imprint","INTERSECT",VERTEX,{"derivedFrom":[subQ4,subQ0]}),-1.0]])],"derivedFrom":subQ4})])]}),makeQuery(id+"F1.opExtrude","SWEPT_FACE",FACE,{"disambiguationData":[OSD([subQ4]),TDD([makeQuery(id+"F0.imprint","IMPRINT",EDGE,{"disambiguationData":[TD([[makeQuery(id+"F0.imprint","INTERSECT",VERTEX,{"derivedFrom":[subQ4,sQuery(id+"F0.wireOp",EDGE,"E0.right")]}),1.0]])],"derivedFrom":subQ4})])]}),makeQuery(id+"F3.opExtrude","CAP_FACE",FACE,{"disambiguationData":[OSD([subQ3,subQ2,subQ1,sQuery(id+"F2.wireOp",EDGE,"E14")])],"isStart":false}),makeQuery(id+"F3.opExtrude","CAP_FACE",FACE,{"disambiguationData":[OSD([subQ3,subQ2,subQ1,sQuery(id+"F2.wireOp",EDGE,"E15")])],"isStart":false}),makeQuery(id+"F3.opExtrude","CAP_FACE",FACE,{"disambiguationData":[OSD([sQuery(id+"F2.wireOp",EDGE,"E16.top"),sQuery(id+"F2.wireOp",EDGE,"E16.left"),sQuery(id+"F2.wireOp",EDGE,"E16.right"),sQuery(id+"F2.wireOp",EDGE,"E17.top"),sQuery(id+"F2.wireOp",EDGE,"E17.left"),sQuery(id+"F2.wireOp",EDGE,"E17.right")])],"isStart":false})]})});}
            var Q2;
            {var subQ0=sQuery(id+"F0.wireOp",EDGE,"E0.left");var subQ1=sQuery(id+"F0.wireOp",EDGE,"E9.right");var subQ2=sQuery(id+"F0.wireOp",EDGE,"E9.left");var subQ3=sQuery(id+"F0.wireOp",EDGE,"E9.top");var subQ4=sQuery(id+"F0.wireOp",EDGE,"E0.top");Q2=makeQuery(id+"F11.boolean.opBoolean","SPLIT",FACE,{"disambiguationData":[TD([makeQuery(id+"F1.opExtrude","SWEPT_FACE",FACE,{"disambiguationData":[OSD([subQ0])]}),makeQuery(id+"F1.opExtrude","SWEPT_FACE",FACE,{"disambiguationData":[OSD([subQ1])]}),makeQuery(id+"F11.opExtrude","SWEPT_FACE",FACE,{"disambiguationData":[OSD([sQuery(id+"F10.wireOp",EDGE,"E36.right")])]}),makeQuery(id+"F11.opExtrude","SWEPT_FACE",FACE,{"disambiguationData":[OSD([sQuery(id+"F10.wireOp",EDGE,"E37.right")])]})])],"derivedFrom":makeQuery(id+"F3.boolean.opBoolean","MERGE",FACE,{"derivedFrom":[makeQuery(id+"F1.opExtrude","SWEPT_FACE",FACE,{"disambiguationData":[OSD([subQ4]),TDD([makeQuery(id+"F0.imprint","IMPRINT",EDGE,{"disambiguationData":[TD([[makeQuery(id+"F0.imprint","INTERSECT",VERTEX,{"derivedFrom":[subQ4,subQ0]}),-1.0]])],"derivedFrom":subQ4})])]}),makeQuery(id+"F1.opExtrude","SWEPT_FACE",FACE,{"disambiguationData":[OSD([subQ4]),TDD([makeQuery(id+"F0.imprint","IMPRINT",EDGE,{"disambiguationData":[TD([[makeQuery(id+"F0.imprint","INTERSECT",VERTEX,{"derivedFrom":[subQ4,sQuery(id+"F0.wireOp",EDGE,"E0.right")]}),1.0]])],"derivedFrom":subQ4})])]}),makeQuery(id+"F3.opExtrude","CAP_FACE",FACE,{"disambiguationData":[OSD([subQ3,subQ2,subQ1,sQuery(id+"F2.wireOp",EDGE,"E14")])],"isStart":false}),makeQuery(id+"F3.opExtrude","CAP_FACE",FACE,{"disambiguationData":[OSD([subQ3,subQ2,subQ1,sQuery(id+"F2.wireOp",EDGE,"E15")])],"isStart":false}),makeQuery(id+"F3.opExtrude","CAP_FACE",FACE,{"disambiguationData":[OSD([sQuery(id+"F2.wireOp",EDGE,"E16.top"),sQuery(id+"F2.wireOp",EDGE,"E16.left"),sQuery(id+"F2.wireOp",EDGE,"E16.right"),sQuery(id+"F2.wireOp",EDGE,"E17.top"),sQuery(id+"F2.wireOp",EDGE,"E17.left"),sQuery(id+"F2.wireOp",EDGE,"E17.right")])],"isStart":false})]})});}
            var Q3;
            {var subQ0=sQuery(id+"F0.wireOp",EDGE,"E0.right");var subQ1=sQuery(id+"F0.wireOp",EDGE,"E9.left");var subQ2=sQuery(id+"F0.wireOp",EDGE,"E9.right");var subQ3=sQuery(id+"F0.wireOp",EDGE,"E9.top");var subQ4=sQuery(id+"F0.wireOp",EDGE,"E0.top");Q3=makeQuery(id+"F11.boolean.opBoolean","SPLIT",FACE,{"disambiguationData":[TD([makeQuery(id+"F1.opExtrude","SWEPT_FACE",FACE,{"disambiguationData":[OSD([subQ0])]}),makeQuery(id+"F1.opExtrude","SWEPT_FACE",FACE,{"disambiguationData":[OSD([subQ1])]}),makeQuery(id+"F11.opExtrude","SWEPT_FACE",FACE,{"disambiguationData":[OSD([sQuery(id+"F10.wireOp",EDGE,"E36.right")])]}),makeQuery(id+"F11.opExtrude","SWEPT_FACE",FACE,{"disambiguationData":[OSD([sQuery(id+"F10.wireOp",EDGE,"E37.right")])]})])],"derivedFrom":makeQuery(id+"F3.boolean.opBoolean","MERGE",FACE,{"derivedFrom":[makeQuery(id+"F1.opExtrude","SWEPT_FACE",FACE,{"disambiguationData":[OSD([subQ4]),TDD([makeQuery(id+"F0.imprint","IMPRINT",EDGE,{"disambiguationData":[TD([[makeQuery(id+"F0.imprint","INTERSECT",VERTEX,{"derivedFrom":[subQ4,sQuery(id+"F0.wireOp",EDGE,"E0.left")]}),-1.0]])],"derivedFrom":subQ4})])]}),makeQuery(id+"F1.opExtrude","SWEPT_FACE",FACE,{"disambiguationData":[OSD([subQ4]),TDD([makeQuery(id+"F0.imprint","IMPRINT",EDGE,{"disambiguationData":[TD([[makeQuery(id+"F0.imprint","INTERSECT",VERTEX,{"derivedFrom":[subQ4,subQ0]}),1.0]])],"derivedFrom":subQ4})])]}),makeQuery(id+"F3.opExtrude","CAP_FACE",FACE,{"disambiguationData":[OSD([subQ3,subQ1,subQ2,sQuery(id+"F2.wireOp",EDGE,"E14")])],"isStart":false}),makeQuery(id+"F3.opExtrude","CAP_FACE",FACE,{"disambiguationData":[OSD([subQ3,subQ1,subQ2,sQuery(id+"F2.wireOp",EDGE,"E15")])],"isStart":false}),makeQuery(id+"F3.opExtrude","CAP_FACE",FACE,{"disambiguationData":[OSD([sQuery(id+"F2.wireOp",EDGE,"E16.top"),sQuery(id+"F2.wireOp",EDGE,"E16.left"),sQuery(id+"F2.wireOp",EDGE,"E16.right"),sQuery(id+"F2.wireOp",EDGE,"E17.top"),sQuery(id+"F2.wireOp",EDGE,"E17.left"),sQuery(id+"F2.wireOp",EDGE,"E17.right")])],"isStart":false})]})});}
            var Q4;
            Q4=makeQuery(id+"F15.boolean.opBoolean","COPY",FACE,{"derivedFrom":makeQuery(id+"F15.opExtrude","CAP_FACE",FACE,{"disambiguationData":[OSD([sQuery(id+"F14.wireOp",EDGE,"E39.bottom"),sQuery(id+"F14.wireOp",EDGE,"E39.top"),sQuery(id+"F14.wireOp",EDGE,"E39.left"),sQuery(id+"F14.wireOp",EDGE,"E39.right")])],"isStart":false})});
            var Q5;
            Q5=makeQuery(id+"F13.boolean.opBoolean","COPY",FACE,{"derivedFrom":makeQuery(id+"F13.opExtrude","CAP_FACE",FACE,{"disambiguationData":[OSD([sQuery(id+"F12.wireOp",EDGE,"E38.bottom"),sQuery(id+"F12.wireOp",EDGE,"E38.top"),sQuery(id+"F12.wireOp",EDGE,"E38.left"),sQuery(id+"F12.wireOp",EDGE,"E38.right")])],"isStart":false})});
            chamfer(context, id + "F16", {"entities" : qUnion([Q0, Q1, Q2, Q3, Q4, Q5]), "width" : 0.4 * mm, "tangentPropagation" : true});
        }
        {
            var Q0;
            Q0=makeQuery(id+"F1.opExtrude","SWEPT_EDGE",EDGE,{"disambiguationData":[OSD([sQuery(id+"F0.wireOp",EDGE,"E11"),sQuery(id+"F0.wireOp",EDGE,"E13")])]});
            var Q1;
            Q1=makeQuery(id+"F1.opExtrude","SWEPT_EDGE",EDGE,{"disambiguationData":[OSD([sQuery(id+"F0.wireOp",EDGE,"E10"),sQuery(id+"F0.wireOp",EDGE,"E12")])]});
            fillet(context, id + "F17", {"entities" : qUnion([Q0, Q1]), "radius" : 0.5 * mm, "tangentPropagation" : true, "allowEdgeOverflow" : false});
        }
    });
